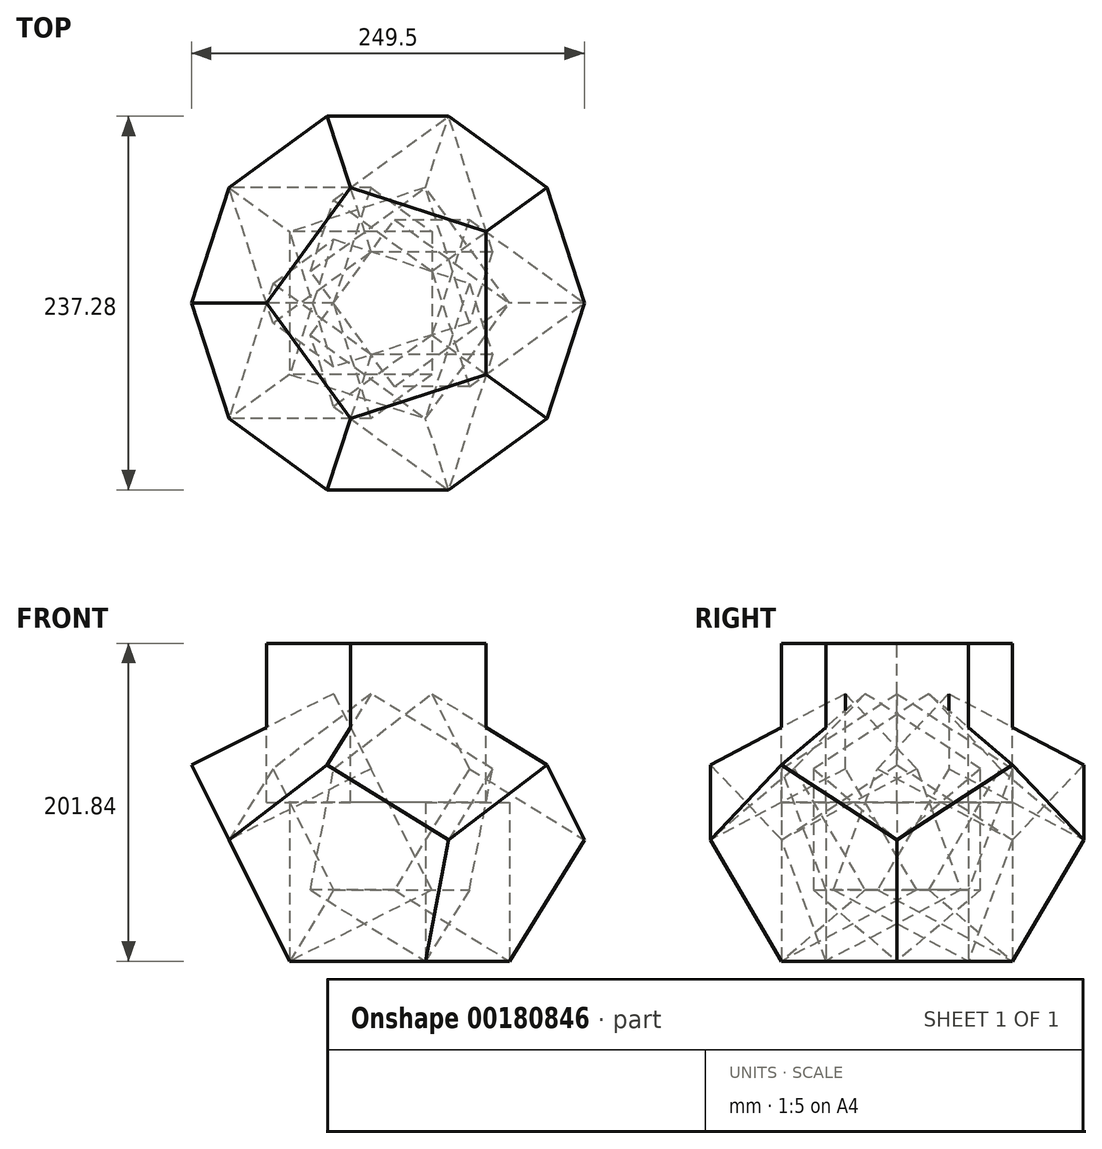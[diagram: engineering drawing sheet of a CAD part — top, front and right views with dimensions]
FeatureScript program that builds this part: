
annotation { "Feature Type Name" : "Feature", "Feature Type Description" : "" }
export const myFeature = defineFeature(function(context is Context, id is Id, definition is map)
    precondition{}
    {
        {
            var Q0;
            Q0=qCreatedBy(makeId("Front.planeOp"),FACE);
            var sketch = newSketch(context, id + "F0", { "sketchPlane" : qUnion([Q0])});
            skLineSegment(sketch, "E0", {"start": v(-77.1, 100.92) * mm, "end": v(62.37, 100.92) * mm});
            skLineSegment(sketch, "E1", {"start": v(-77.1, 100.92) * mm, "end": v(77.1, -100.92) * mm, "construction": true});
            skLineSegment(sketch, "E2", {"start": v(77.1, -100.92) * mm, "end": v(-62.37, -100.92) * mm});
            skLineSegment(sketch, "E3", {"start": v(62.37, 100.92) * mm, "end": v(124.75, -23.82) * mm});
            skLineSegment(sketch, "E4", {"start": v(124.75, -23.82) * mm, "end": v(77.1, -100.92) * mm});
            skLineSegment(sketch, "E5", {"start": v(-62.37, -100.92) * mm, "end": v(-124.75, 23.82) * mm});
            skLineSegment(sketch, "E6", {"start": v(-77.1, 100.92) * mm, "end": v(-124.75, 23.82) * mm});
            skCircle(sketch, "E7", {"center": v(0, 0) * mm, "radius": 77.1 * mm, "construction": true});
            skLineSegment(sketch, "E8", {"start": v(-77.1, 0) * mm, "end": v(-23.82, 73.32) * mm, "construction": true});
            skLineSegment(sketch, "E9", {"start": v(-23.82, 73.32) * mm, "end": v(62.37, 45.32) * mm, "construction": true});
            skLineSegment(sketch, "E10", {"start": v(62.37, 45.32) * mm, "end": v(62.37, -45.32) * mm, "construction": true});
            skLineSegment(sketch, "E11", {"start": v(62.37, -45.32) * mm, "end": v(-23.82, -73.32) * mm, "construction": true});
            skLineSegment(sketch, "E12", {"start": v(-23.82, -73.32) * mm, "end": v(-77.1, 0) * mm, "construction": true});
            skLineSegment(sketch, "E13", {"start": v(-77.1, 0) * mm, "end": v(62.37, 0) * mm, "construction": true});
            skLineSegment(sketch, "E14", {"start": v(-124.75, 23.82) * mm, "end": v(124.75, -23.82) * mm, "construction": true});
            skSolve(sketch);
        }
        {
            var Q0;
            Q0=sQuery(id+"F0.wireOp",VERTEX,"E5.start");
            var Q1;
            Q1=qCreatedBy(makeId("Top.planeOp"),FACE);
            cPlane(context, id + "F1", {"entities" : qUnion([Q0, Q1]), "cplaneType" : CPlaneType.PLANE_POINT, "offset" : 25.4 * mm, "width" : 152.4 * mm, "height" : 152.4 * mm});
        }
        {
            var Q0;
            Q0=qCreatedBy(id+"F1.planeOp",FACE);
            var sketch = newSketch(context, id + "F2", { "sketchPlane" : qUnion([Q0])});
            skCircle(sketch, "E15", {"center": v(0, 0) * mm, "radius": 77.1 * mm, "construction": true});
            skLineSegment(sketch, "E16", {"start": v(77.1, 0) * mm, "end": v(23.82, 73.32) * mm});
            skLineSegment(sketch, "E17", {"start": v(23.82, 73.32) * mm, "end": v(-62.37, 45.32) * mm});
            skLineSegment(sketch, "E18", {"start": v(-62.37, 45.32) * mm, "end": v(-62.37, -45.32) * mm});
            skLineSegment(sketch, "E19", {"start": v(-62.37, -45.32) * mm, "end": v(23.82, -73.32) * mm});
            skLineSegment(sketch, "E20", {"start": v(23.82, -73.32) * mm, "end": v(77.1, 0) * mm});
            skSolve(sketch);
        }
        {
            var Q0;
            Q0 = qSketchRegion(id + "F2", true);
            var Q1;
            Q1=qCreatedBy(makeId("Top.planeOp"),FACE);
            extrude(context, id + "F3", {"entities" : qUnion([Q0]), "endBound" : BoundingType.UP_TO_SURFACE, "endBoundEntityFace" : qUnion([Q1]), "depth" : 61.98 * mm});
        }
        {
            var Q0;
            Q0=sQuery(id+"F0.wireOp",VERTEX,"E7.center");
            var Q1;
            Q1=makeQuery(id+"F3.opExtrude","CAP_VERTEX",VERTEX,{"disambiguationData":[OSD([sQuery(id+"F2.wireOp",EDGE,"E17"),sQuery(id+"F2.wireOp",EDGE,"E18")])],"isStart":true});
            var Q2;
            Q2=makeQuery(id+"F3.opExtrude","CAP_VERTEX",VERTEX,{"disambiguationData":[OSD([sQuery(id+"F2.wireOp",EDGE,"E18"),sQuery(id+"F2.wireOp",EDGE,"E19")])],"isStart":true});
            cPlane(context, id + "F4", {"entities" : qUnion([Q0, Q1, Q2]), "cplaneType" : CPlaneType.THREE_POINT, "offset" : 25.4 * mm, "width" : 152.4 * mm, "height" : 152.4 * mm});
        }
        {
            var Q0;
            Q0=makeQuery(id+"F3.opExtrude","SWEPT_BODY",BODY,{"disambiguationData":[OSD([sQuery(id+"F2.wireOp",EDGE,"E16"),sQuery(id+"F2.wireOp",EDGE,"E17"),sQuery(id+"F2.wireOp",EDGE,"E18"),sQuery(id+"F2.wireOp",EDGE,"E19"),sQuery(id+"F2.wireOp",EDGE,"E20")])]});
            var Q1;
            Q1=qCreatedBy(id+"F4.planeOp",FACE);
            mirror(context, id + "F5", {"entities" : qUnion([Q0]), "mirrorPlane" : qUnion([Q1])});
        }
        {
            var Q0;
            Q0=qCreatedBy(makeId("Front.planeOp"),FACE);
            var sketch = newSketch(context, id + "F6", { "sketchPlane" : qUnion([Q0])});
            skLineSegment(sketch, "E21", {"start": v(0, 101.02) * mm, "end": v(0, 0) * mm, "construction": true});
            skSolve(sketch);
        }
        {
            var Q0;
            Q0=makeQuery(id+"F5.opPattern","COPY",BODY,{"derivedFrom":makeQuery(id+"F3.opExtrude","SWEPT_BODY",BODY,{"disambiguationData":[OSD([sQuery(id+"F2.wireOp",EDGE,"E16"),sQuery(id+"F2.wireOp",EDGE,"E17"),sQuery(id+"F2.wireOp",EDGE,"E18"),sQuery(id+"F2.wireOp",EDGE,"E19"),sQuery(id+"F2.wireOp",EDGE,"E20")])]}),"instanceName":"1"});
            var Q1;
            Q1=sQuery(id+"F6.wireOp",EDGE,"E21");
            circularPattern(context, id + "F7", {"entities" : qUnion([Q0]), "axis" : qUnion([Q1]), "angle" : 72 * degree, "instanceCount" : 5});
        }
        {
            var Q0;
            Q0=makeQuery(id+"F3.opExtrude","SWEPT_BODY",BODY,{"disambiguationData":[OSD([sQuery(id+"F2.wireOp",EDGE,"E16"),sQuery(id+"F2.wireOp",EDGE,"E17"),sQuery(id+"F2.wireOp",EDGE,"E18"),sQuery(id+"F2.wireOp",EDGE,"E19"),sQuery(id+"F2.wireOp",EDGE,"E20")])]});
            var Q1;
            Q1=qCreatedBy(makeId("Top.planeOp"),FACE);
            mirror(context, id + "F8", {"entities" : qUnion([Q0]), "mirrorPlane" : qUnion([Q1])});
        }
        {
            var Q0;
            Q0=makeQuery(id+"F8.opPattern","COPY",BODY,{"derivedFrom":makeQuery(id+"F3.opExtrude","SWEPT_BODY",BODY,{"disambiguationData":[OSD([sQuery(id+"F2.wireOp",EDGE,"E16"),sQuery(id+"F2.wireOp",EDGE,"E17"),sQuery(id+"F2.wireOp",EDGE,"E18"),sQuery(id+"F2.wireOp",EDGE,"E19"),sQuery(id+"F2.wireOp",EDGE,"E20")])]}),"instanceName":"1"});
            var Q1;
            Q1=sQuery(id+"F6.wireOp",EDGE,"E21");
            transform(context, id + "F9", {"entities" : qUnion([Q0]), "transformType" : TransformType.ROTATION, "transformAxis" : qUnion([Q1]), "angle" : 36 * degree, "makeCopy" : false});
        }
    });
